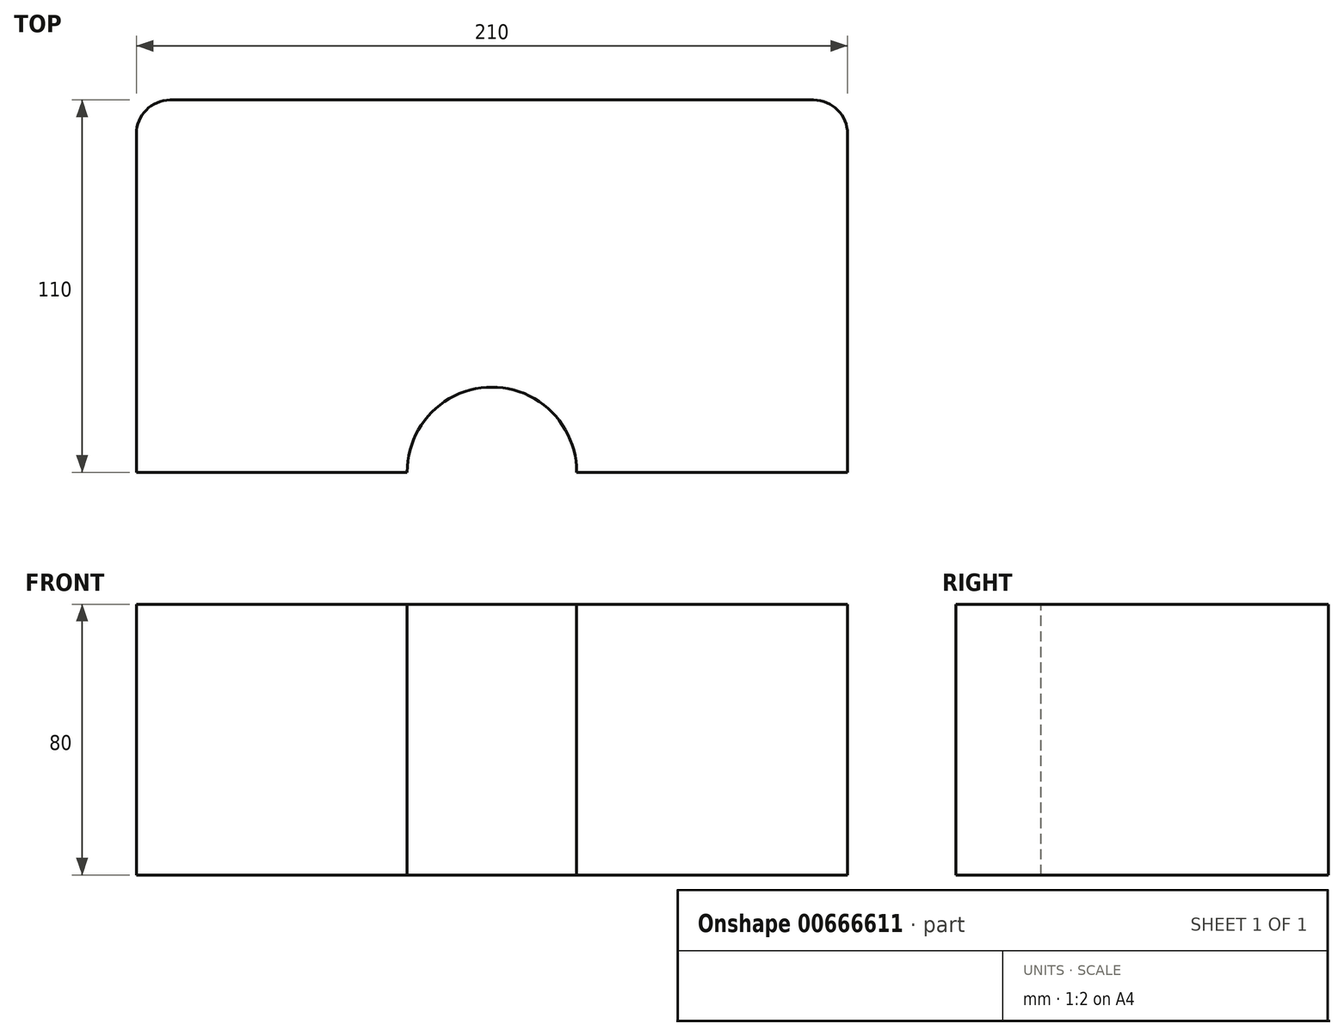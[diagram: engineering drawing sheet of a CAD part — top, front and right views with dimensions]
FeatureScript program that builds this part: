
annotation { "Feature Type Name" : "Feature", "Feature Type Description" : "" }
export const myFeature = defineFeature(function(context is Context, id is Id, definition is map)
    precondition{}
    {
        {
            var Q0;
            Q0=qCreatedBy(makeId("Top.planeOp"),FACE);
            var sketch = newSketch(context, id + "F0", { "sketchPlane" : qUnion([Q0])});
            skLineSegment(sketch, "E0.bottom", {"start": v(-72.34, 38.45) * mm, "end": v(137.66, 38.45) * mm});
            skLineSegment(sketch, "E0.top", {"start": v(-72.34, -71.55) * mm, "end": v(137.66, -71.55) * mm});
            skLineSegment(sketch, "E0.left", {"start": v(-72.34, 38.45) * mm, "end": v(-72.34, -71.55) * mm});
            skLineSegment(sketch, "E0.right", {"start": v(137.66, 38.45) * mm, "end": v(137.66, -71.55) * mm});
            skSolve(sketch);
        }
        {
            var Q0;
            Q0=makeQuery(id+"F0.imprint","IMPRINT",FACE,{"disambiguationData":[TD([[makeQuery(id+"F0.imprint","IMPRINT",EDGE,{"derivedFrom":sQuery(id+"F0.wireOp",EDGE,"E0.bottom")}),-1.0]])]});
            extrude(context, id + "F1", {"entities" : qUnion([Q0]), "depth" : 80 * mm, "offsetDistance" : 25 * mm});
        }
        {
            var Q0;
            Q0=makeQuery(id+"F1.opExtrude","CAP_FACE",FACE,{"disambiguationData":[OSD([sQuery(id+"F0.wireOp",EDGE,"E0.bottom"),sQuery(id+"F0.wireOp",EDGE,"E0.top"),sQuery(id+"F0.wireOp",EDGE,"E0.left"),sQuery(id+"F0.wireOp",EDGE,"E0.right")])],"isStart":false});
            var sketch = newSketch(context, id + "F2", { "sketchPlane" : qUnion([Q0])});
            skLineSegment(sketch, "E1", {"start": v(137.66, -71.55) * mm, "end": v(57.66, -71.55) * mm});
            skLineSegment(sketch, "E2", {"start": v(-72.34, -71.55) * mm, "end": v(7.66, -71.55) * mm});
            skArc(sketch, "E3", {"start": v(57.66, -71.55) * mm, "mid": v(32.66, -46.4) * mm, "end": v(7.66, -71.55) * mm});
            skSolve(sketch);
        }
        {
            var Q0;
            {var subQ0=sQuery(id+"F2.wireOp",EDGE,"E3");Q0=makeQuery(id+"F2.imprint","IMPRINT",FACE,{"disambiguationData":[TD([[makeQuery(id+"F2.imprint","IMPRINT",EDGE,{"derivedFrom":subQ0}),1.0]])]});}
            extrude(context, id + "F3", {"entities" : qUnion([Q0]), "operationType" : NewBodyOperationType.REMOVE, "oppositeDirection" : true, "depth" : 80 * mm, "offsetDistance" : 25 * mm});
        }
        {
            var Q0;
            Q0=makeQuery(id+"F1.opExtrude","SWEPT_EDGE",EDGE,{"disambiguationData":[OSD([sQuery(id+"F0.wireOp",EDGE,"E0.bottom"),sQuery(id+"F0.wireOp",EDGE,"E0.left")])]});
            var Q1;
            Q1=makeQuery(id+"F1.opExtrude","SWEPT_EDGE",EDGE,{"disambiguationData":[OSD([sQuery(id+"F0.wireOp",EDGE,"E0.bottom"),sQuery(id+"F0.wireOp",EDGE,"E0.right")])]});
            fillet(context, id + "F4", {"entities" : qUnion([Q0, Q1]), "radius" : 10 * mm, "tangentPropagation" : true, "allowEdgeOverflow" : false});
        }
    });
